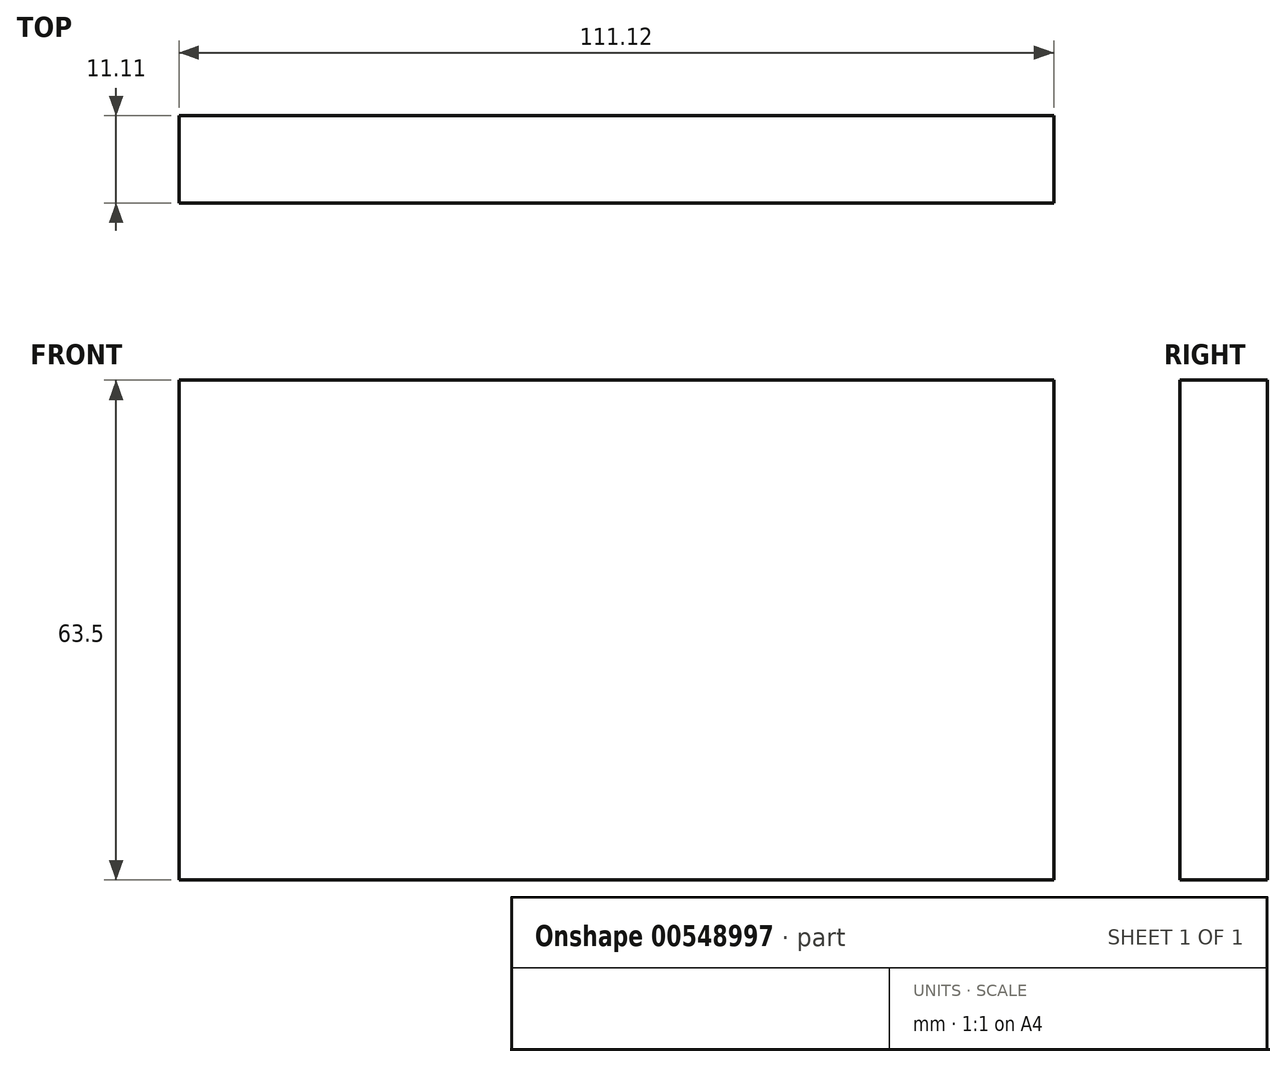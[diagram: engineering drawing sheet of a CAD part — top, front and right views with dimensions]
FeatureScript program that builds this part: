
annotation { "Feature Type Name" : "Feature", "Feature Type Description" : "" }
export const myFeature = defineFeature(function(context is Context, id is Id, definition is map)
    precondition{}
    {
        {
            var Q0;
            Q0=qCreatedBy(makeId("Front.planeOp"),FACE);
            var sketch = newSketch(context, id + "F0", { "sketchPlane" : qUnion([Q0])});
            skLineSegment(sketch, "E0.bottom", {"start": v(55.56, -31.75) * mm, "end": v(-55.56, -31.75) * mm});
            skLineSegment(sketch, "E0.top", {"start": v(55.56, 31.75) * mm, "end": v(-55.56, 31.75) * mm});
            skLineSegment(sketch, "E0.left", {"start": v(55.56, -31.75) * mm, "end": v(55.56, 31.75) * mm});
            skLineSegment(sketch, "E0.right", {"start": v(-55.56, -31.75) * mm, "end": v(-55.56, 31.75) * mm});
            skPoint(sketch, "E0.middle", {"position": v(0, 0) * mm});
            skSolve(sketch);
        }
        {
            var Q0;
            Q0 = qSketchRegion(id + "F0", true);
            extrude(context, id + "F1", {"entities" : qUnion([Q0]), "depth" : 11.1 * mm, "offsetDistance" : 25.4 * mm});
        }
    });
